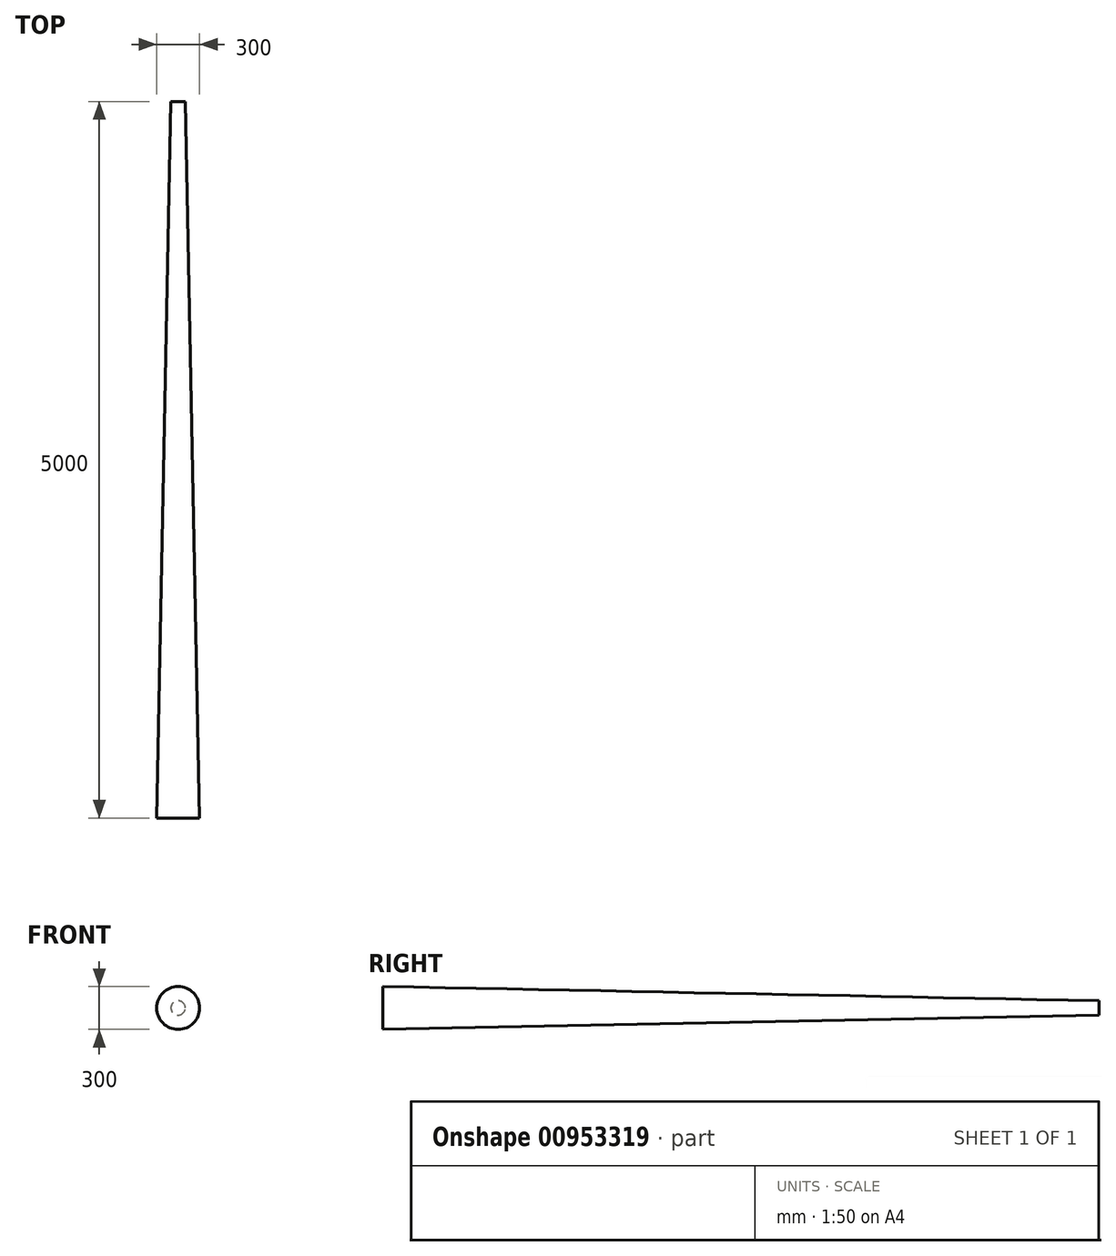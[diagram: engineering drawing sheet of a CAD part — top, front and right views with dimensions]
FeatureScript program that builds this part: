
annotation { "Feature Type Name" : "Feature", "Feature Type Description" : "" }
export const myFeature = defineFeature(function(context is Context, id is Id, definition is map)
    precondition{}
    {
        {
            var Q0;
            Q0=qCreatedBy(makeId("Top.planeOp"),FACE);
            var sketch = newSketch(context, id + "F0", { "sketchPlane" : qUnion([Q0])});
            skLineSegment(sketch, "E0", {"start": v(0, 2503.43) * mm, "end": v(0, -2496.57) * mm});
            skLineSegment(sketch, "E1", {"start": v(0, 2503.43) * mm, "end": v(50, 2503.43) * mm});
            skLineSegment(sketch, "E2", {"start": v(0, -2496.57) * mm, "end": v(150, -2496.57) * mm});
            skLineSegment(sketch, "E3", {"start": v(50, 2503.43) * mm, "end": v(150, -2496.57) * mm});
            skSolve(sketch);
        }
        {
            var Q0;
            Q0=makeQuery(id+"F0.imprint","IMPRINT",FACE,{"disambiguationData":[TD([[makeQuery(id+"F0.imprint","IMPRINT",EDGE,{"derivedFrom":sQuery(id+"F0.wireOp",EDGE,"E0")}),1.0]])]});
            var Q1;
            Q1=sQuery(id+"F0.wireOp",EDGE,"E0");
            revolve(context, id + "F1", {"surfaceOperationType" : NewSurfaceOperationType.NEW, "entities" : qUnion([Q0]), "axis" : qUnion([Q1]), "revolveType" : RevolveType.FULL});
        }
    });
